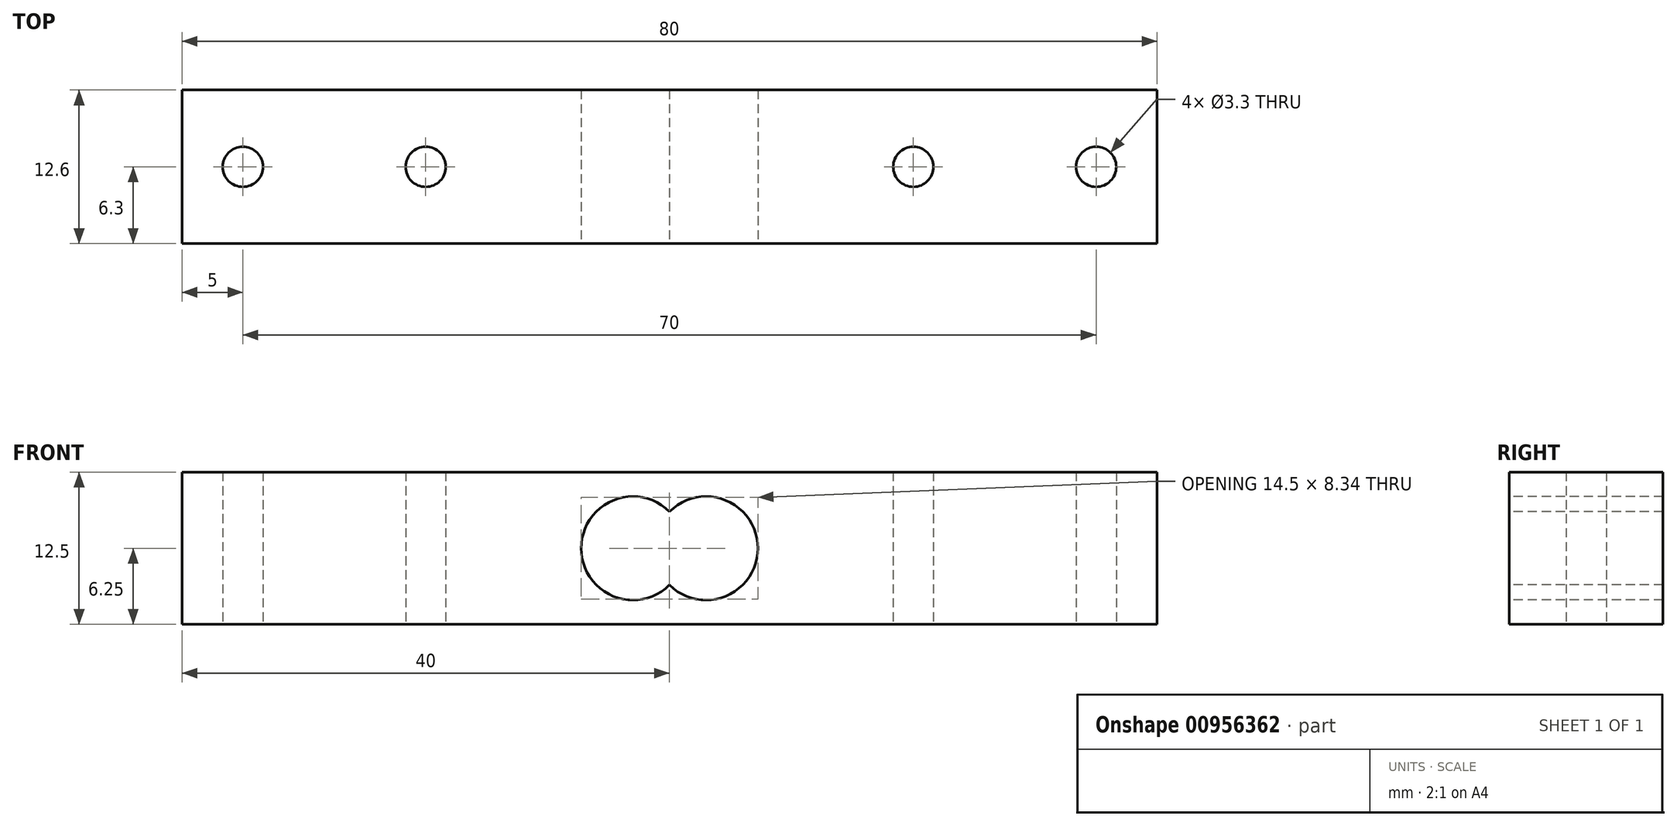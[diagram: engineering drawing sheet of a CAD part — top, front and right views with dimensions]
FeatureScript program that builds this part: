
annotation { "Feature Type Name" : "Feature", "Feature Type Description" : "" }
export const myFeature = defineFeature(function(context is Context, id is Id, definition is map)
    precondition{}
    {
        {
            var Q0;
            Q0=qCreatedBy(makeId("Top.planeOp"),FACE);
            var sketch = newSketch(context, id + "F0", { "sketchPlane" : qUnion([Q0])});
            skLineSegment(sketch, "E0.bottom", {"start": v(-40, -6.3) * mm, "end": v(40, -6.3) * mm});
            skLineSegment(sketch, "E0.top", {"start": v(-40, 6.3) * mm, "end": v(40, 6.3) * mm});
            skLineSegment(sketch, "E0.left", {"start": v(-40, -6.3) * mm, "end": v(-40, 6.3) * mm});
            skLineSegment(sketch, "E0.right", {"start": v(40, -6.3) * mm, "end": v(40, 6.3) * mm});
            skLineSegment(sketch, "E1", {"start": v(-40, 0) * mm, "end": v(40, 0) * mm, "construction": true});
            skLineSegment(sketch, "E2", {"start": v(0, -6.3) * mm, "end": v(0, 6.3) * mm, "construction": true});
            skPoint(sketch, "E3", {"position": v(-35, 0) * mm});
            skPoint(sketch, "E4", {"position": v(-20, 0) * mm});
            skPoint(sketch, "E5.MirrorP", {"position": v(35, 0) * mm});
            skPoint(sketch, "E6.MirrorP", {"position": v(20, 0) * mm});
            skSolve(sketch);
        }
        {
            var Q0;
            Q0=makeQuery(id+"F0.imprint","IMPRINT",FACE,{"disambiguationData":[TD([[makeQuery(id+"F0.imprint","IMPRINT",EDGE,{"derivedFrom":sQuery(id+"F0.wireOp",EDGE,"E0.bottom")}),1.0]])]});
            extrude(context, id + "F1", {"entities" : qUnion([Q0]), "depth" : 12.5 * mm, "offsetDistance" : 25 * mm});
        }
        {
            var Q0;
            Q0=makeQuery(id+"F1.opExtrude","SWEPT_FACE",FACE,{"disambiguationData":[OSD([sQuery(id+"F0.wireOp",EDGE,"E0.bottom")])]});
            var sketch = newSketch(context, id + "F2", { "sketchPlane" : qUnion([Q0])});
            skLineSegment(sketch, "E7", {"start": v(-40, 6.25) * mm, "end": v(40, 6.25) * mm, "construction": true});
            skLineSegment(sketch, "E8", {"start": v(0, 12.5) * mm, "end": v(0, 0) * mm, "construction": true});
            skCircle(sketch, "E9", {"center": v(3, 6.25) * mm, "radius": 4.25 * mm});
            skCircle(sketch, "E10.MirrorC", {"center": v(-3, 6.25) * mm, "radius": 4.25 * mm});
            skSolve(sketch);
        }
        {
            var Q0;
            Q0 = qSketchRegion(id + "F2", true);
            extrude(context, id + "F3", {"entities" : qUnion([Q0]), "operationType" : NewBodyOperationType.REMOVE, "endBound" : BoundingType.UP_TO_NEXT, "oppositeDirection" : true, "depth" : 25 * mm, "offsetDistance" : 25 * mm});
        }
        {
            var Q0;
            Q0=sQuery(id+"F0.wireOp",VERTEX,"E4");
            var Q1;
            Q1=sQuery(id+"F0.wireOp",VERTEX,"E3");
            var Q2;
            Q2=sQuery(id+"F0.wireOp",VERTEX,"E6.MirrorP");
            var Q3;
            Q3=sQuery(id+"F0.wireOp",VERTEX,"E5.MirrorP");
            var Q4;
            Q4=makeQuery(id+"F1.opExtrude","SWEPT_BODY",BODY,{"disambiguationData":[OSD([sQuery(id+"F0.wireOp",EDGE,"E0.bottom"),sQuery(id+"F0.wireOp",EDGE,"E0.top"),sQuery(id+"F0.wireOp",EDGE,"E0.left"),sQuery(id+"F0.wireOp",EDGE,"E0.right")])]});
            hole(context, id + "F4", {"style" : HoleStyle.SIMPLE, "endStyle" : HoleEndStyle.THROUGH, "oppositeDirection" : true, "standardTappedOrClearance" : lookupTablePath({ "standard" : "ISO", "engagement" : "75%", "pitch" : "0.7 mm", "size" : "M4", "type" : "Tapped" }), "standardBlindInLast" : lookupTablePath({ "standard" : "ISO", "fit" : "Normal", "engagement" : "75%", "pitch" : "0.7 mm", "size" : "M4", "type" : "Clearance & tapped" }), "holeDiameter" : 3.3 * mm, "majorDiameter" : 4 * mm, "showTappedDepth" : true, "isTappedThrough" : true, "tappedDepth" : 12 * mm, "tapClearance" : 3, "locations" : qUnion([Q0, Q1, Q2, Q3]), "scope" : qUnion([Q4])});
        }
    });
